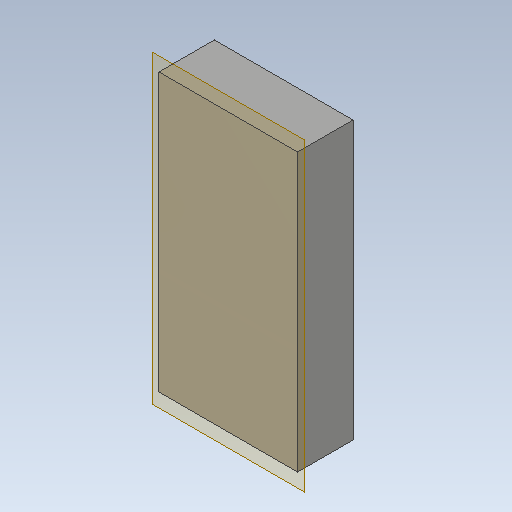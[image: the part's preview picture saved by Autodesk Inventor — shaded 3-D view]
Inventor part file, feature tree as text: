
AUTODESK INVENTOR PART (.ipt)
format: ipt  version: 2020.1 (Build 241239000, 239)  size: 105,984 bytes
history: native  units: mm
features: other x3, sketch x2, plane x1, extrude x1, hole x1, projected_geometry x1
ambient origin geometry x8: Origin, YZ Plane, XZ Plane, XY Plane, X Axis, Y Axis, Z Axis, Center Point
bodies: Solid1 (feature_tree)
feature tree (9):
  plane  "Work Plane1"
  extrude  "Extrusion1"  Depth=20.0mm
  hole  "Hole1"  [1 undecoded]
  sketch  "Sketch1"  dims[d0=10.0mm d1=20.0mm]
  sketch  "Sketch2"  dims[d2=4.0mm d3=0.0mm d4=5.0mm d5=6.0mm d6=8.0mm d7=2.0mm d8=90.0deg d9=8.0mm d10=20.594885mm]
  projected_geometry  "Projected Loop1"
  parser-record x1  (decoder bookkeeping rows leaked as tree rows — omitted from the tree; the rows remain in map.json)
  other  "håndfang.iam"
  other  "stang:2"
note: 1 required parameter value undecoded (feature->parameter linkage not recoverable at this tier; creation-order binding heuristic only, values carry confidence <= 0.55)
note: 1 file-system path scrubbed to <path> (originals preserved in map.json)
